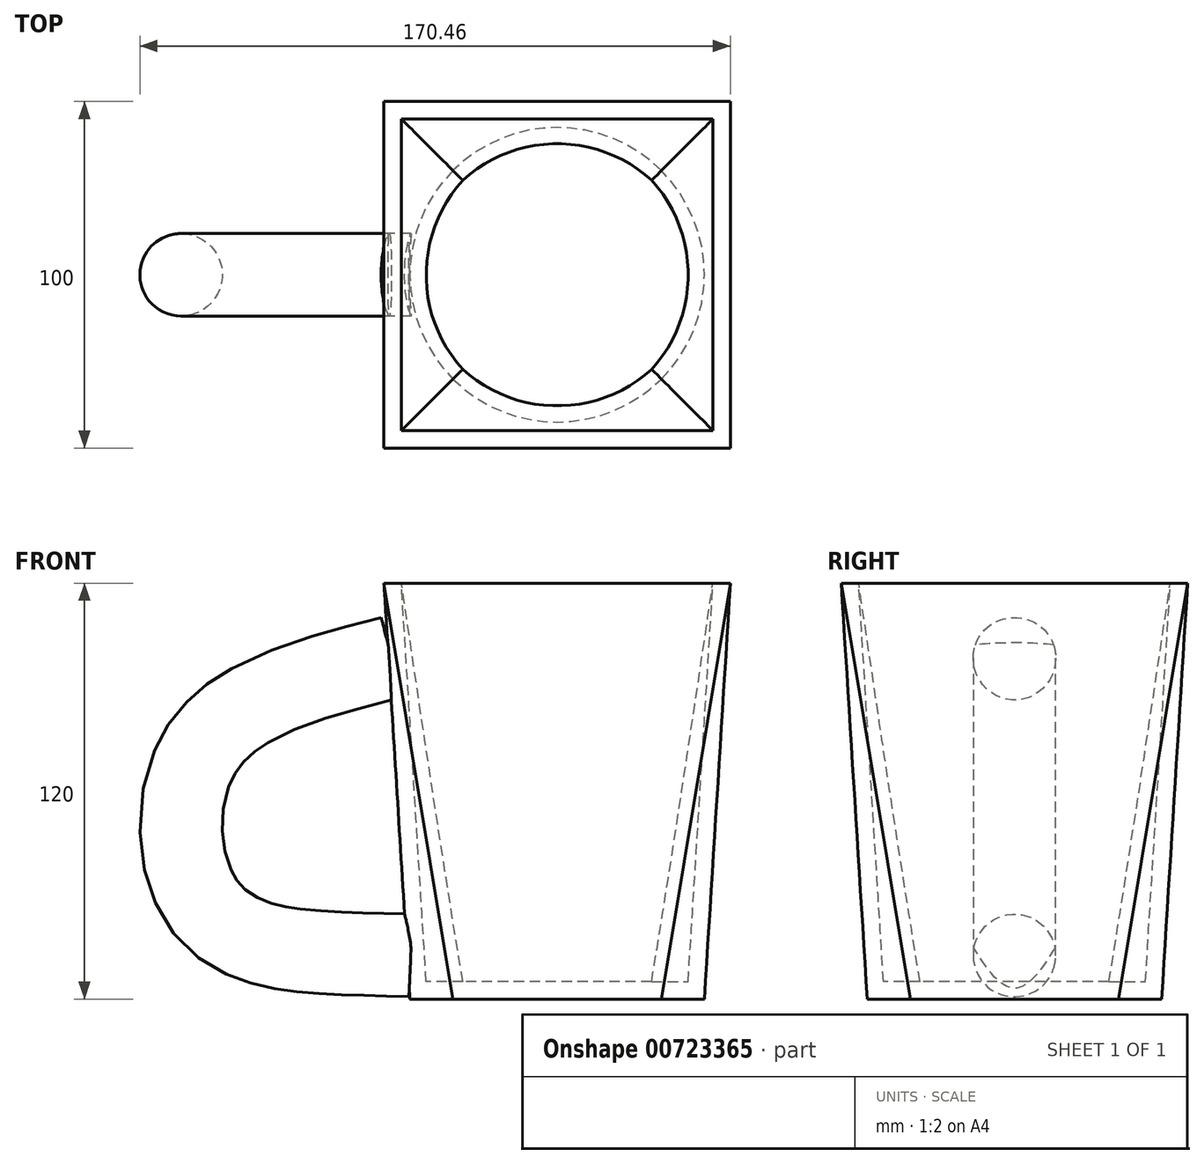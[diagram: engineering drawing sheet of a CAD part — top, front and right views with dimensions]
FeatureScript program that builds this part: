
annotation { "Feature Type Name" : "Feature", "Feature Type Description" : "" }
export const myFeature = defineFeature(function(context is Context, id is Id, definition is map)
    precondition{}
    {
        {
            var Q0;
            Q0=qCreatedBy(makeId("Top.planeOp"),FACE);
            cPlane(context, id + "F0", {"entities" : qUnion([Q0]), "cplaneType" : CPlaneType.OFFSET, "offset" : 120 * mm, "width" : 150 * mm, "height" : 150 * mm});
        }
        {
            var Q0;
            Q0=qCreatedBy(makeId("Top.planeOp"),FACE);
            var sketch = newSketch(context, id + "F1", { "sketchPlane" : qUnion([Q0])});
            skCircle(sketch, "E0", {"center": v(0, 0) * mm, "radius": 42.5 * mm});
            skSolve(sketch);
        }
        {
            var Q0;
            Q0=qCreatedBy(id+"F0.planeOp",FACE);
            var sketch = newSketch(context, id + "F2", { "sketchPlane" : qUnion([Q0])});
            skLineSegment(sketch, "E1.bottom", {"start": v(-50, -50) * mm, "end": v(50, -50) * mm});
            skLineSegment(sketch, "E1.top", {"start": v(-50, 50) * mm, "end": v(50, 50) * mm});
            skLineSegment(sketch, "E1.left", {"start": v(-50, -50) * mm, "end": v(-50, 50) * mm});
            skLineSegment(sketch, "E1.right", {"start": v(50, -50) * mm, "end": v(50, 50) * mm});
            skPoint(sketch, "E1.middle", {"position": v(0, 0) * mm});
            skSolve(sketch);
        }
        {
            var Q0;
            Q0=makeQuery(id+"F1.imprint","IMPRINT",FACE,{"disambiguationData":[TD([[makeQuery(id+"F1.imprint","IMPRINT",EDGE,{"derivedFrom":sQuery(id+"F1.wireOp",EDGE,"E0")}),1.0]])]});
            var Q1;
            Q1=makeQuery(id+"F2.imprint","IMPRINT",FACE,{"disambiguationData":[TD([[makeQuery(id+"F2.imprint","IMPRINT",EDGE,{"derivedFrom":sQuery(id+"F2.wireOp",EDGE,"E1.bottom")}),1.0]])]});
            loft(context, id + "F3", {"sheetProfilesArray" : [{ "sheetProfileEntities" : qUnion([Q0]) }, { "sheetProfileEntities" : qUnion([Q1]) }]});
        }
        {
            var Q0;
            Q0=makeQuery(id+"F3.opLoft","CAP_FACE",FACE,{"disambiguationData":[OSD([makeQuery(id+"F2.imprint","IMPRINT",FACE,{"disambiguationData":[TD([[makeQuery(id+"F2.imprint","IMPRINT",EDGE,{"derivedFrom":sQuery(id+"F2.wireOp",EDGE,"E1.bottom")}),1.0]])]})])],"isStart":true});
            shell(context, id + "F4", {"entities" : qUnion([Q0]), "thickness" : 5 * mm});
        }
        {
            var Q0;
            Q0=qCreatedBy(makeId("Front.planeOp"),FACE);
            var sketch = newSketch(context, id + "F5", { "sketchPlane" : qUnion([Q0])});
            skFitSpline(sketch, "E2", {"points": [v(-47.85, 98.57) * mm, v(-100.93, 74.58) * mm, v(-106.35, 35.85) * mm, v(-87.86, 16.9) * mm, v(-42.26, 12.55) * mm], "startDerivative": vector(-208.56, -53.24) * mm, "endDerivative": vector(186.1, -8.64) * mm});
            skSolve(sketch);
        }
        {
            var Q0;
            Q0=sQuery(id+"F5.wireOp",VERTEX,"E2.0.internal");
            var Q1;
            Q1=sQuery(id+"F5.wireOp",EDGE,"E2");
            cPlane(context, id + "F6", {"entities" : qUnion([Q0, Q1]), "cplaneType" : CPlaneType.CURVE_POINT, "offset" : 25 * mm, "width" : 150 * mm, "height" : 150 * mm});
        }
        {
            var Q0;
            Q0=qCreatedBy(id+"F6.planeOp",FACE);
            var sketch = newSketch(context, id + "F7", { "sketchPlane" : qUnion([Q0])});
            skCircle(sketch, "E3", {"center": v(0, 107.35) * mm, "radius": 11.9 * mm});
            skSolve(sketch);
        }
        {
            var Q0;
            Q0=makeQuery(id+"F7.imprint","IMPRINT",FACE,{"disambiguationData":[TD([[makeQuery(id+"F7.imprint","IMPRINT",EDGE,{"derivedFrom":sQuery(id+"F7.wireOp",EDGE,"E3")}),1.0]])]});
            var Q1;
            Q1=sQuery(id+"F5.wireOp",EDGE,"E2");
            sweep(context, id + "F8", {"operationType" : NewBodyOperationType.ADD, "profiles" : qUnion([Q0]), "path" : qUnion([Q1])});
        }
    });
